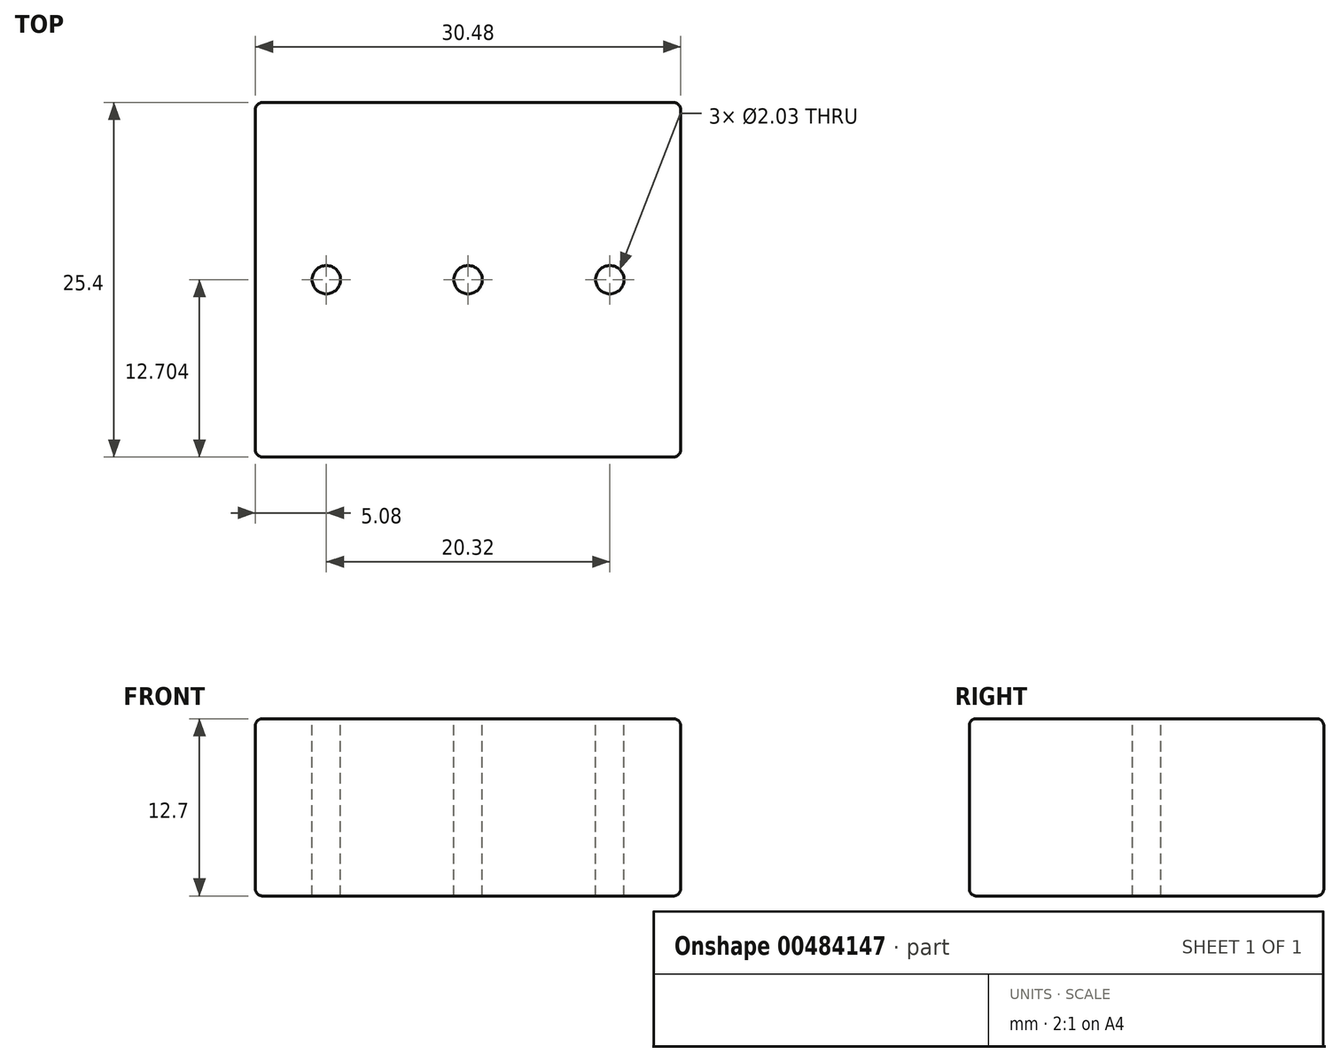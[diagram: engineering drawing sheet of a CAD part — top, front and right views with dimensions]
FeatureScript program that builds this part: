
annotation { "Feature Type Name" : "Feature", "Feature Type Description" : "" }
export const myFeature = defineFeature(function(context is Context, id is Id, definition is map)
    precondition{}
    {
        {
            var Q0;
            Q0=qCreatedBy(makeId("Top.planeOp"),FACE);
            var sketch = newSketch(context, id + "F0", { "sketchPlane" : qUnion([Q0])});
            skLineSegment(sketch, "E0", {"start": v(-61.95, 18.43) * mm, "end": v(-31.47, 18.43) * mm});
            skLineSegment(sketch, "E1", {"start": v(-61.95, -6.97) * mm, "end": v(-61.95, 18.43) * mm});
            skLineSegment(sketch, "E2", {"start": v(-36.55, 5.73) * mm, "end": v(-46.71, 5.73) * mm, "construction": true});
            skLineSegment(sketch, "E3", {"start": v(-46.71, 5.73) * mm, "end": v(-56.87, 5.73) * mm, "construction": true});
            skCircle(sketch, "E4", {"center": v(-56.87, 5.73) * mm, "radius": 1.02 * mm});
            skCircle(sketch, "E5", {"center": v(-46.71, 5.73) * mm, "radius": 1.02 * mm});
            skCircle(sketch, "E6", {"center": v(-36.55, 5.73) * mm, "radius": 1.02 * mm});
            skLineSegment(sketch, "E7.trimOffspring", {"start": v(-31.47, 5.73) * mm, "end": v(-36.55, 5.73) * mm, "construction": true});
            skLineSegment(sketch, "E8.trimOffspring", {"start": v(-31.47, -6.97) * mm, "end": v(-61.95, -6.97) * mm});
            skPoint(sketch, "E9.orphan", {"position": v(-11.15, -6.97) * mm});
            skPoint(sketch, "E10.trimOffspring.start.orphan", {"position": v(-11.15, 18.43) * mm});
            skPoint(sketch, "E11.end.orphan", {"position": v(39.65, -6.97) * mm});
            skPoint(sketch, "E11.start.orphan", {"position": v(39.65, 18.43) * mm});
            skPoint(sketch, "E12.orphan", {"position": v(-11.15, 5.73) * mm});
            skPoint(sketch, "E13.start.orphan", {"position": v(-26.4, 5.73) * mm});
            skLineSegment(sketch, "E14", {"start": v(-31.47, 18.43) * mm, "end": v(-31.47, -6.97) * mm});
            skSolve(sketch);
        }
        {
            var Q0;
            Q0=makeQuery(id+"F0.imprint","IMPRINT",FACE,{"disambiguationData":[TD([[makeQuery(id+"F0.imprint","IMPRINT",EDGE,{"derivedFrom":sQuery(id+"F0.wireOp",EDGE,"E0")}),-1.0]])]});
            extrude(context, id + "F1", {"entities" : qUnion([Q0]), "oppositeDirection" : true, "depth" : 12.7 * mm});
        }
        {
            var Q0;
            Q0=makeQuery(id+"F1.opExtrude","CAP_EDGE",EDGE,{"disambiguationData":[OSD([sQuery(id+"F0.wireOp",EDGE,"E0")])],"isStart":true});
            var Q1;
            Q1=makeQuery(id+"F1.opExtrude","CAP_EDGE",EDGE,{"disambiguationData":[OSD([sQuery(id+"F0.wireOp",EDGE,"E11")])],"isStart":true});
            var Q2;
            Q2=makeQuery(id+"F1.opExtrude","CAP_EDGE",EDGE,{"disambiguationData":[OSD([sQuery(id+"F0.wireOp",EDGE,"8Y4KWfmv-g5fn-rBJA-KAog-qUrvxMS0yLDE")])],"isStart":true});
            var Q3;
            Q3=makeQuery(id+"F1.opExtrude","CAP_EDGE",EDGE,{"disambiguationData":[OSD([sQuery(id+"F0.wireOp",EDGE,"E1")])],"isStart":true});
            var Q4;
            Q4=makeQuery(id+"F1.opExtrude","SWEPT_EDGE",EDGE,{"disambiguationData":[OSD([sQuery(id+"F0.wireOp",EDGE,"8Y4KWfmv-g5fn-rBJA-KAog-qUrvxMS0yLDE"),sQuery(id+"F0.wireOp",EDGE,"E1")])]});
            var Q5;
            Q5=makeQuery(id+"F1.opExtrude","SWEPT_EDGE",EDGE,{"disambiguationData":[OSD([sQuery(id+"F0.wireOp",EDGE,"E11"),sQuery(id+"F0.wireOp",EDGE,"8Y4KWfmv-g5fn-rBJA-KAog-qUrvxMS0yLDE")])]});
            var Q6;
            Q6=makeQuery(id+"F1.opExtrude","SWEPT_EDGE",EDGE,{"disambiguationData":[OSD([sQuery(id+"F0.wireOp",EDGE,"E0"),sQuery(id+"F0.wireOp",EDGE,"E11")])]});
            var Q7;
            Q7=makeQuery(id+"F1.opExtrude","SWEPT_EDGE",EDGE,{"disambiguationData":[OSD([sQuery(id+"F0.wireOp",EDGE,"E0"),sQuery(id+"F0.wireOp",EDGE,"E1")])]});
            var Q8;
            Q8=makeQuery(id+"F1.opExtrude","CAP_EDGE",EDGE,{"disambiguationData":[OSD([sQuery(id+"F0.wireOp",EDGE,"E11")])],"isStart":false});
            var Q9;
            Q9=makeQuery(id+"F1.opExtrude","CAP_EDGE",EDGE,{"disambiguationData":[OSD([sQuery(id+"F0.wireOp",EDGE,"E0")])],"isStart":false});
            var Q10;
            Q10=makeQuery(id+"F1.opExtrude","CAP_EDGE",EDGE,{"disambiguationData":[OSD([sQuery(id+"F0.wireOp",EDGE,"E1")])],"isStart":false});
            var Q11;
            Q11=makeQuery(id+"F1.opExtrude","CAP_EDGE",EDGE,{"disambiguationData":[OSD([sQuery(id+"F0.wireOp",EDGE,"8Y4KWfmv-g5fn-rBJA-KAog-qUrvxMS0yLDE")])],"isStart":false});
            var Q12;
            Q12=makeQuery(id+"F1.opExtrude","CAP_EDGE",EDGE,{"disambiguationData":[OSD([sQuery(id+"F0.wireOp",EDGE,"E14")])],"isStart":true});
            var Q13;
            Q13=makeQuery(id+"F1.opExtrude","CAP_EDGE",EDGE,{"disambiguationData":[OSD([sQuery(id+"F0.wireOp",EDGE,"E8.trimOffspring")])],"isStart":true});
            var Q14;
            Q14=makeQuery(id+"F1.opExtrude","SWEPT_EDGE",EDGE,{"disambiguationData":[OSD([sQuery(id+"F0.wireOp",EDGE,"E8.trimOffspring"),sQuery(id+"F0.wireOp",EDGE,"E14")])]});
            var Q15;
            Q15=makeQuery(id+"F1.opExtrude","CAP_EDGE",EDGE,{"disambiguationData":[OSD([sQuery(id+"F0.wireOp",EDGE,"E14")])],"isStart":false});
            var Q16;
            Q16=makeQuery(id+"F1.opExtrude","CAP_EDGE",EDGE,{"disambiguationData":[OSD([sQuery(id+"F0.wireOp",EDGE,"E8.trimOffspring")])],"isStart":false});
            fillet(context, id + "F2", {"entities" : qUnion([Q0, Q1, Q2, Q3, Q4, Q5, Q6, Q7, Q8, Q9, Q10, Q11, Q12, Q13, Q14, Q15, Q16]), "radius" : 0.5 * mm, "tangentPropagation" : true, "allowEdgeOverflow" : false});
        }
    });
